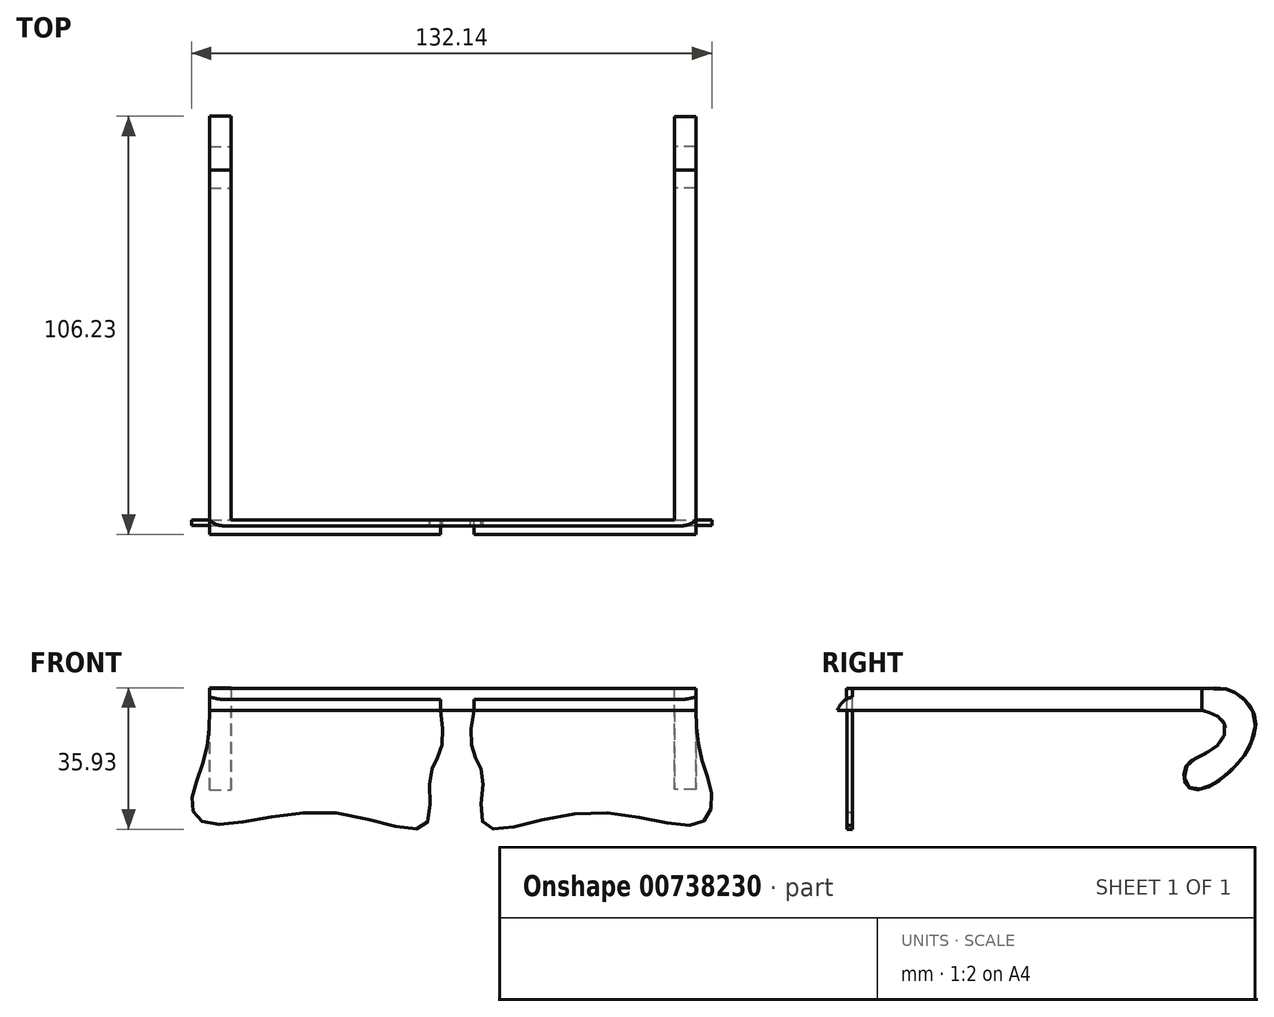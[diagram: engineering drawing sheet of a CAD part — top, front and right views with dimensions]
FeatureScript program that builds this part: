
annotation { "Feature Type Name" : "Feature", "Feature Type Description" : "" }
export const myFeature = defineFeature(function(context is Context, id is Id, definition is map)
    precondition{}
    {
        {
            var Q0;
            Q0=qCreatedBy(makeId("Front.planeOp"),FACE);
            var sketch = newSketch(context, id + "F0", { "sketchPlane" : qUnion([Q0])});
            skLineSegment(sketch, "E0", {"start": v(-62.7, 5.5) * mm, "end": v(-62.7, 0) * mm});
            skLineSegment(sketch, "E1", {"start": v(-62.7, 0) * mm, "end": v(-57.18, 0) * mm});
            skLineSegment(sketch, "E2", {"start": v(-57.18, 0) * mm, "end": v(-57.18, 5.5) * mm});
            skLineSegment(sketch, "E3", {"start": v(-57.18, 5.5) * mm, "end": v(-62.7, 5.5) * mm});
            skLineSegment(sketch, "E4", {"start": v(55.4, 5.5) * mm, "end": v(55.4, 0) * mm});
            skLineSegment(sketch, "E5", {"start": v(55.4, 0) * mm, "end": v(60.92, 0) * mm});
            skLineSegment(sketch, "E6", {"start": v(60.92, 0) * mm, "end": v(60.92, 5.5) * mm});
            skLineSegment(sketch, "E7", {"start": v(60.92, 5.5) * mm, "end": v(55.4, 5.5) * mm});
            skSolve(sketch);
        }
        {
            var Q0;
            Q0=makeQuery(id+"F0.imprint","IMPRINT",FACE,{"disambiguationData":[TD([[makeQuery(id+"F0.imprint","IMPRINT",EDGE,{"derivedFrom":sQuery(id+"F0.wireOp",EDGE,"E0")}),1.0]])]});
            var Q1;
            Q1=makeQuery(id+"F0.imprint","IMPRINT",FACE,{"disambiguationData":[TD([[makeQuery(id+"F0.imprint","IMPRINT",EDGE,{"derivedFrom":sQuery(id+"F0.wireOp",EDGE,"E4")}),1.0]])]});
            extrude(context, id + "F1", {"entities" : qUnion([Q0, Q1]), "oppositeDirection" : true, "depth" : 88.9 * mm, "offsetDistance" : 25.4 * mm});
        }
        {
            var Q0;
            Q0=makeQuery(id+"F1.opExtrude","CAP_FACE",FACE,{"disambiguationData":[OSD([sQuery(id+"F0.wireOp",EDGE,"E0"),sQuery(id+"F0.wireOp",EDGE,"E1"),sQuery(id+"F0.wireOp",EDGE,"E2"),sQuery(id+"F0.wireOp",EDGE,"E3")])],"isStart":true});
            var sketch = newSketch(context, id + "F2", { "sketchPlane" : qUnion([Q0])});
            skPoint(sketch, "E8.0", {"position": v(60.92, 0) * mm});
            skLineSegment(sketch, "E9.bottom", {"start": v(60.92, 0) * mm, "end": v(-62.7, 0) * mm});
            skLineSegment(sketch, "E9.top", {"start": v(60.92, 5.5) * mm, "end": v(-62.7, 5.5) * mm});
            skLineSegment(sketch, "E9.left", {"start": v(60.92, 0) * mm, "end": v(60.92, 5.5) * mm});
            skLineSegment(sketch, "E9.right", {"start": v(-62.7, 0) * mm, "end": v(-62.7, 5.5) * mm});
            skSolve(sketch);
        }
        {
            var Q0;
            Q0 = qSketchRegion(id + "F2", true);
            extrude(context, id + "F3", {"entities" : qUnion([Q0]), "depth" : 1.52 * mm, "offsetDistance" : 25.4 * mm});
        }
        {
            var Q0;
            Q0=qCreatedBy(makeId("Front.planeOp"),FACE);
            var sketch = newSketch(context, id + "F4", { "sketchPlane" : qUnion([Q0])});
            skPoint(sketch, "E10.0", {"position": v(-62.7, 0) * mm});
            skPoint(sketch, "E11.0", {"position": v(60.92, 0) * mm});
            skFitSpline(sketch, "E12", {"points": [v(-62.7, 0) * mm, v(-64.08, -12.74) * mm, v(-67.21, -23.7) * mm, v(-62.7, -28.84) * mm, v(-32.1, -25.98) * mm, v(-7.92, -29.33) * mm, v(-6.65, -16.97) * mm, v(-4.12, -10.69) * mm, v(-3.94, 0) * mm], "startDerivative": vector(-2.14, -106.47) * mm, "endDerivative": vector(-17.68, 109.34) * mm});
            skFitSpline(sketch, "E13", {"points": [v(4.58, 0) * mm, v(4.34, -10.91) * mm, v(6.76, -17.08) * mm, v(7.32, -29.33) * mm, v(33.37, -25.98) * mm, v(61.71, -28.84) * mm, v(64.9, -22.2) * mm, v(62.08, -11.14) * mm, v(60.92, 0) * mm], "startDerivative": vector(-29.24, -113.04) * mm, "endDerivative": vector(-3.32, 98.7) * mm});
            skLineSegment(sketch, "E14", {"start": v(-62.7, 0) * mm, "end": v(-3.94, 0) * mm});
            skLineSegment(sketch, "E15", {"start": v(4.58, 0) * mm, "end": v(60.92, 0) * mm});
            skSolve(sketch);
        }
        {
            var Q0;
            Q0=qCreatedBy(makeId("Front.planeOp"),FACE);
            var sketch = newSketch(context, id + "F5", { "sketchPlane" : qUnion([Q0])});
            skFitSpline(sketch, "E16", {"points": [v(-3.58, 0) * mm, v(-2.87, -4.73) * mm, v(-3.4, -10) * mm, v(-4.58, -13.18) * mm, v(-4.34, -13.75) * mm, v(-3.3, -12.99) * mm, v(-1.64, -9.62) * mm, v(0, -7.67) * mm, v(1.92, -9.52) * mm, v(3.2, -12.46) * mm, v(4.3, -13.5) * mm], "startDerivative": vector(6.7, -33.98) * mm, "endDerivative": vector(13.39, -4.94) * mm});
            skFitSpline(sketch, "E17", {"points": [v(4.3, -13.5) * mm, v(4.72, -12.94) * mm, v(3.54, -9.47) * mm, v(3.35, -4.5) * mm, v(4.3, 0) * mm], "startDerivative": vector(5.07, 3.6) * mm, "endDerivative": vector(3.65, 14.68) * mm});
            skSolve(sketch);
        }
        {
            var Q0;
            Q0 = qSketchRegion(id + "F5", true);
            var Q1;
            Q1=sQuery(id+"F5.wireOp",EDGE,"E16");
            var Q2;
            Q2=sQuery(id+"F5.wireOp",EDGE,"E17");
            extrude(context, id + "F6", {"entities" : qUnion([Q0]), "bodyType" : ToolBodyType.SURFACE, "surfaceEntities" : qUnion([Q1, Q2]), "depth" : 0.64 * mm, "offsetDistance" : 25.4 * mm});
        }
        {
            var Q0;
            Q0=makeQuery(id+"F3.opExtrude","CAP_FACE",FACE,{"disambiguationData":[OSD([sQuery(id+"F2.wireOp",EDGE,"E9.bottom"),sQuery(id+"F2.wireOp",EDGE,"E9.top"),sQuery(id+"F2.wireOp",EDGE,"E9.left"),sQuery(id+"F2.wireOp",EDGE,"E9.right")])],"isStart":false});
            var sketch = newSketch(context, id + "F7", { "sketchPlane" : qUnion([Q0])});
            skLineSegment(sketch, "E18.bottom", {"start": v(-62.7, 2.75) * mm, "end": v(-3.93, 2.75) * mm});
            skLineSegment(sketch, "E18.top", {"start": v(-62.7, 0) * mm, "end": v(-3.93, 0) * mm});
            skLineSegment(sketch, "E18.left", {"start": v(-62.7, 2.75) * mm, "end": v(-62.7, 0) * mm});
            skLineSegment(sketch, "E18.right", {"start": v(-3.93, 2.75) * mm, "end": v(-3.93, 0) * mm});
            skLineSegment(sketch, "E19.bottom", {"start": v(4.58, 0) * mm, "end": v(60.92, 0) * mm});
            skLineSegment(sketch, "E19.top", {"start": v(4.58, 2.75) * mm, "end": v(60.92, 2.75) * mm});
            skLineSegment(sketch, "E19.left", {"start": v(4.58, 0) * mm, "end": v(4.58, 2.75) * mm});
            skLineSegment(sketch, "E19.right", {"start": v(60.92, 0) * mm, "end": v(60.92, 2.75) * mm});
            skSolve(sketch);
        }
        {
            var Q0;
            Q0 = qSketchRegion(id + "F7", true);
            extrude(context, id + "F8", {"entities" : qUnion([Q0]), "operationType" : NewBodyOperationType.ADD, "depth" : 2.41 * mm, "offsetDistance" : 25.4 * mm});
        }
        {
            var Q0;
            Q0=makeQuery(id+"F8.opExtrude","CAP_EDGE",EDGE,{"disambiguationData":[OSD([sQuery(id+"F7.wireOp",EDGE,"E18.bottom")])],"isStart":false});
            var Q1;
            Q1=makeQuery(id+"F8.opExtrude","CAP_EDGE",EDGE,{"disambiguationData":[OSD([sQuery(id+"F7.wireOp",EDGE,"E19.top")])],"isStart":false});
            fillet(context, id + "F9", {"entities" : qUnion([Q0, Q1]), "radius" : 5.08 * mm, "tangentPropagation" : true, "allowEdgeOverflow" : false});
        }
        {
            var Q0;
            Q0=makeQuery(id+"F1.opExtrude","SWEPT_FACE",FACE,{"disambiguationData":[OSD([sQuery(id+"F0.wireOp",EDGE,"E6")])]});
            var sketch = newSketch(context, id + "F10", { "sketchPlane" : qUnion([Q0])});
            skFitSpline(sketch, "E20", {"points": [v(88.9, 0) * mm, v(90.87, -0.7) * mm, v(94, -2.47) * mm, v(94.45, -6.72) * mm, v(89.52, -11.23) * mm, v(85.21, -13.8) * mm, v(84.8, -18.76) * mm, v(88.9, -19.96) * mm, v(95.1, -16.27) * mm, v(100.32, -10.24) * mm, v(102.25, -1.59) * mm, v(98.22, 3.82) * mm, v(94.18, 5.46) * mm, v(88.9, 5.5) * mm], "startDerivative": vector(32.35, -8.37) * mm, "endDerivative": vector(-58.38, 9.88) * mm});
            skSolve(sketch);
        }
        {
            var Q0;
            Q0=makeQuery(id+"F10.imprint","IMPRINT",FACE,{"disambiguationData":[TD([[makeQuery(id+"F10.imprint","IMPRINT",EDGE,{"derivedFrom":sQuery(id+"F10.wireOp",EDGE,"E20")}),1.0]])]});
            extrude(context, id + "F11", {"entities" : qUnion([Q0]), "oppositeDirection" : true, "depth" : 5.5 * mm, "offsetDistance" : 25.4 * mm});
        }
        {
            var Q0;
            Q0=makeQuery(id+"F1.opExtrude","SWEPT_FACE",FACE,{"disambiguationData":[OSD([sQuery(id+"F0.wireOp",EDGE,"E0")])]});
            var sketch = newSketch(context, id + "F12", { "sketchPlane" : qUnion([Q0])});
            skFitSpline(sketch, "E21", {"points": [v(-88.9, 5.5) * mm, v(-94.9, 5.5) * mm, v(-98.17, 3.98) * mm, v(-101.1, 1.04) * mm, v(-102.51, -2.68) * mm, v(-101.67, -7.48) * mm, v(-99.35, -11.88) * mm, v(-95.74, -15.83) * mm, v(-90.44, -19.5) * mm, v(-86.43, -20.06) * mm, v(-84.62, -18.65) * mm, v(-84.28, -16.17) * mm, v(-85.13, -13.69) * mm, v(-87.61, -12) * mm, v(-91.85, -9.74) * mm, v(-94.73, -6.3) * mm, v(-94.61, -3.75) * mm, v(-93.48, -1.95) * mm, v(-88.9, 0) * mm], "startDerivative": vector(-94.8, 7.04) * mm, "endDerivative": vector(86.76, 27.92) * mm});
            skSolve(sketch);
        }
        {
            var Q0;
            Q0=makeQuery(id+"F12.imprint","IMPRINT",FACE,{"disambiguationData":[TD([[makeQuery(id+"F12.imprint","IMPRINT",EDGE,{"derivedFrom":sQuery(id+"F12.wireOp",EDGE,"E21")}),1.0]])]});
            var Q1;
            Q1=sQuery(id+"F12.wireOp",EDGE,"E21");
            extrude(context, id + "F13", {"entities" : qUnion([Q0]), "surfaceEntities" : qUnion([Q1]), "oppositeDirection" : true, "depth" : 5.5 * mm, "offsetDistance" : 25.4 * mm});
        }
        {
            var Q0;
            Q0=makeQuery(id+"F3.opExtrude","CAP_EDGE",EDGE,{"disambiguationData":[OSD([sQuery(id+"F2.wireOp",EDGE,"E9.right")])],"isStart":false});
            fillet(context, id + "F14", {"entities" : qUnion([Q0]), "radius" : 5.08 * mm, "tangentPropagation" : true, "allowEdgeOverflow" : false});
        }
        {
            var Q0;
            Q0=makeQuery(id+"F3.opExtrude","CAP_EDGE",EDGE,{"disambiguationData":[OSD([sQuery(id+"F2.wireOp",EDGE,"E9.left")])],"isStart":false});
            fillet(context, id + "F15", {"entities" : qUnion([Q0]), "radius" : 5.08 * mm, "tangentPropagation" : true, "allowEdgeOverflow" : false});
        }
        {
            var Q0;
            Q0 = qSketchRegion(id + "F4", true);
            extrude(context, id + "F16", {"entities" : qUnion([Q0]), "operationType" : NewBodyOperationType.ADD, "depth" : 1.4 * mm, "offsetDistance" : 25.4 * mm});
        }
    });
